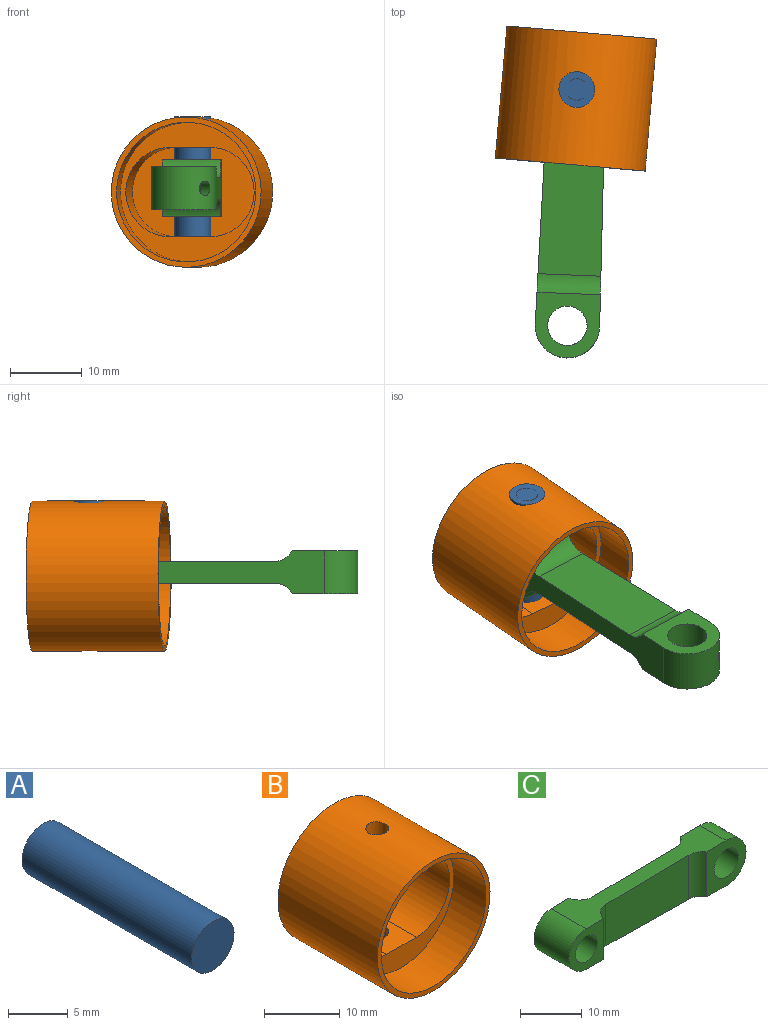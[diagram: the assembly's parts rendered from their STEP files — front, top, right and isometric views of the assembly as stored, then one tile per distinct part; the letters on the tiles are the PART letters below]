
ASSEMBLY  parts=3 mates=2
PART A: 3 faces, bbox 5x20x5 mm
  f0: cylinder r=2.5mm len=20mm, axis (0,1,0), area 314.2mm2, adj f1,f2
  f1: plane 5x5mm, normal (0,-1,0), area 19.6mm2, adj f0
  f2: plane 5x5mm, normal (0,1,0), area 19.6mm2, adj f0
PART B: 12 faces, bbox 21x18.5x21 mm
  f0: cylinder r=10.5mm len=21mm, axis (0,1,0), area 1206.3mm2, adj f1,f2,f10,f11
  f1: plane 21x21mm, normal (0,-1,0), area 47.7mm2, adj f0,f4
  f2: plane 21x21mm, normal (0,1,0), area 346.4mm2, adj f0
  f3: plane 19.5x19.5mm, normal (0,-1,0), area 107.2mm2, adj f4,f6,f7,f8,f9
  f4: cylinder r=9.75mm len=19.5mm, axis (0,-1,0), area 367.6mm2, adj f1,f3
  f5: plane 18x12.5mm, normal (0,-1,0), area 191.5mm2, adj f6,f7,f8,f9
  f6: cylinder r=6.25mm len=12.5mm, axis (0,1,0), area 206.2mm2, adj f3,f5,f7,f9
  f7: plane 10.5x5.5mm, normal (0,0,1), area 50.7mm2, adj f3,f5,f6,f8,f11
  f8: cylinder r=6.25mm len=12.5mm, axis (0,1,0), area 206.2mm2, adj f3,f5,f7,f9
  f9: plane 10.5x5.5mm, normal (0,0,-1), area 50.7mm2, adj f3,f5,f6,f8,f10
  f10: cylinder r=1.5mm len=4.25mm, axis (0,0,1), area 39.5mm2, adj f0,f9
  f11: cylinder r=1.5mm len=4.25mm, axis (0,0,1), area 39.5mm2, adj f0,f7
PART C: 17 faces, bbox 41.5x8x9 mm
  f0: cylinder r=4.5mm len=9mm, axis (0,1,0), area 82.5mm2, adj f4,f6,f7,f8,f16
  f1: cylinder r=2.75mm len=6mm, axis (0,-1,0), area 100.5mm2, adj f7,f8,f16
  f2: plane 18.94x8.79mm, normal (0,-1,0), area 161mm2, adj f4,f6,f12,f14
  f3: plane 18.94x8.79mm, normal (0,1,0), area 161mm2, adj f4,f6,f13,f15
  f4: plane 33.01x8.01mm, normal (-0.02,0,1), area 138.5mm2, adj f0,f2,f3,f5,f7,f8,f9,f10
  f5: cylinder r=4mm len=8mm, axis (0,1,0), area 99.6mm2, adj f4,f6,f9,f10
  f6: plane 33.01x8.01mm, normal (-0.02,0,-1), area 138.5mm2, adj f0,f2,f3,f5,f7,f8,f9,f10
  f7: plane 9x9mm, normal (0,1,0), area 48.2mm2, adj f0,f1,f4,f6,f15
  f8: plane 9x9mm, normal (0,-1,0), area 48.2mm2, adj f0,f1,f4,f6,f14
  f9: plane 8.12x8mm, normal (0,1,0), area 37.7mm2, adj f4,f5,f6,f11,f13
  f10: plane 8.12x8mm, normal (0,-1,0), area 37.7mm2, adj f4,f5,f6,f11,f12
  f11: cylinder r=2.5mm len=8mm, axis (0,-1,0), area 125.7mm2, adj f9,f10
  f12: cylinder r=3mm len=8.21mm, axis (0,0,-1), area 34.4mm2, adj f2,f4,f6,f10
  f13: cylinder r=3mm len=8.21mm, axis (0,0,-1), area 34.4mm2, adj f3,f4,f6,f9
  f14: cylinder r=3mm len=8.86mm, axis (0,0,-1), area 27.7mm2, adj f2,f4,f6,f8
  f15: cylinder r=3mm len=8.86mm, axis (0,0,-1), area 27.7mm2, adj f3,f4,f6,f7
  f16: cylinder r=1mm len=2.79mm, axis (0.71,0,0.71), area 11.2mm2, adj f0,f1
PLACE A rot(axis=(-1,0.02,-0.02),90deg) t=(38.73,22.46,-9.47)mm
PLACE B rot(axis=(0,0,-1),5deg) t=(39.42,30.43,0)mm fixed
PLACE C rot(axis=(-0.56,0.58,-0.58),121.3deg) t=(38.73,22.46,0.53)mm
MATE fastened C.f11 <-> A.f0  axis (0,0,1) through (38.73,22.46,0.53)mm
MATE revolute A.f0 <-> B.f10  axis (0,0,1) through (38.73,22.46,10.53)mm
